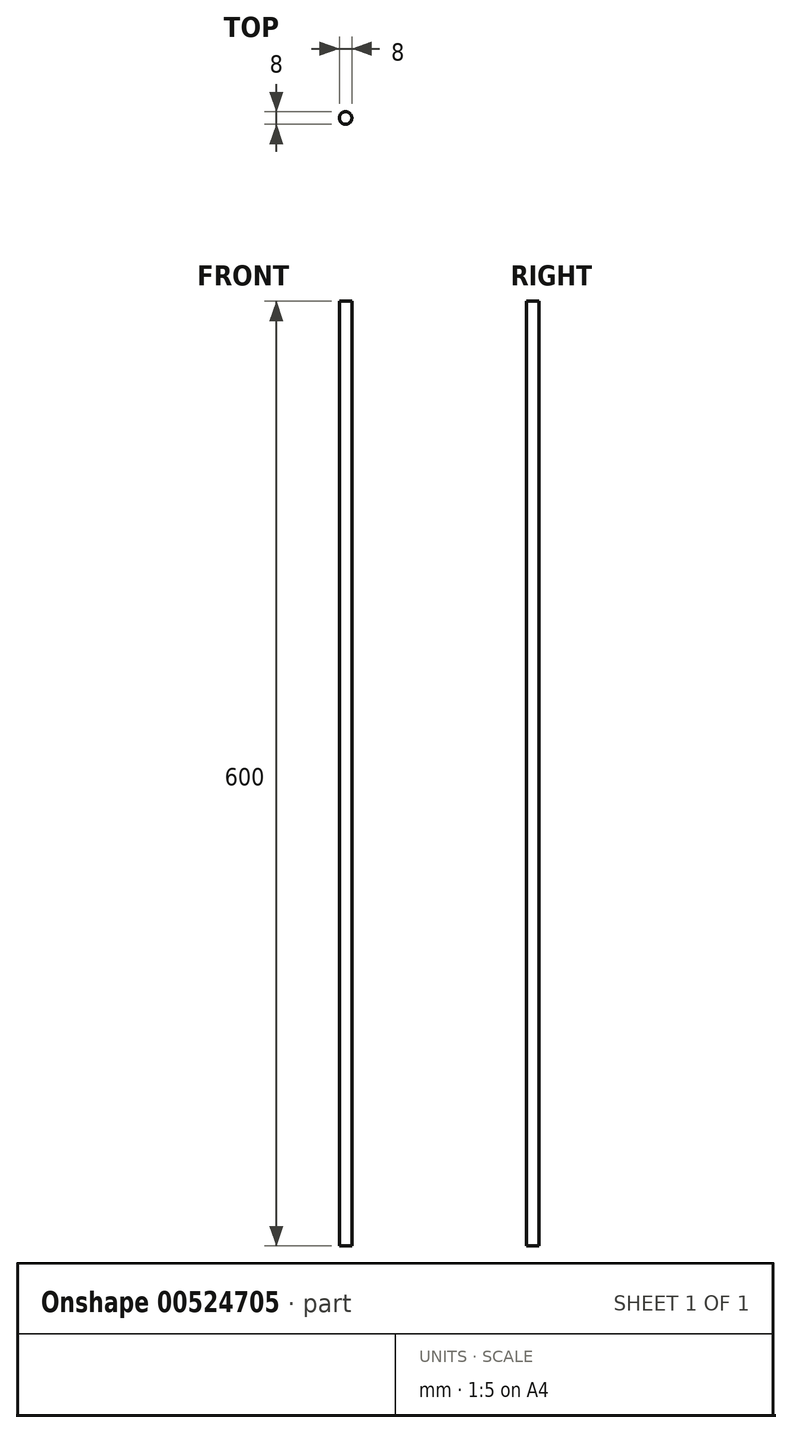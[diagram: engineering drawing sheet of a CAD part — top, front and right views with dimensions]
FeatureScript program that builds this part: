
annotation { "Feature Type Name" : "Feature", "Feature Type Description" : "" }
export const myFeature = defineFeature(function(context is Context, id is Id, definition is map)
    precondition{}
    {
        {
            var Q0;
            Q0=qCreatedBy(makeId("Top.planeOp"),FACE);
            var sketch = newSketch(context, id + "F0", { "sketchPlane" : qUnion([Q0])});
            skCircle(sketch, "E0", {"center": v(0, 0) * mm, "radius": 4 * mm});
            skSolve(sketch);
        }
        {
            var Q0;
            Q0=makeQuery(id+"F0.imprint","IMPRINT",FACE,{"disambiguationData":[TD([[makeQuery(id+"F0.imprint","IMPRINT",EDGE,{"derivedFrom":sQuery(id+"F0.wireOp",EDGE,"E0")}),1.0]])]});
            extrude(context, id + "F1", {"entities" : qUnion([Q0]), "depth" : 600 * mm, "offsetDistance" : 25 * mm});
        }
    });
